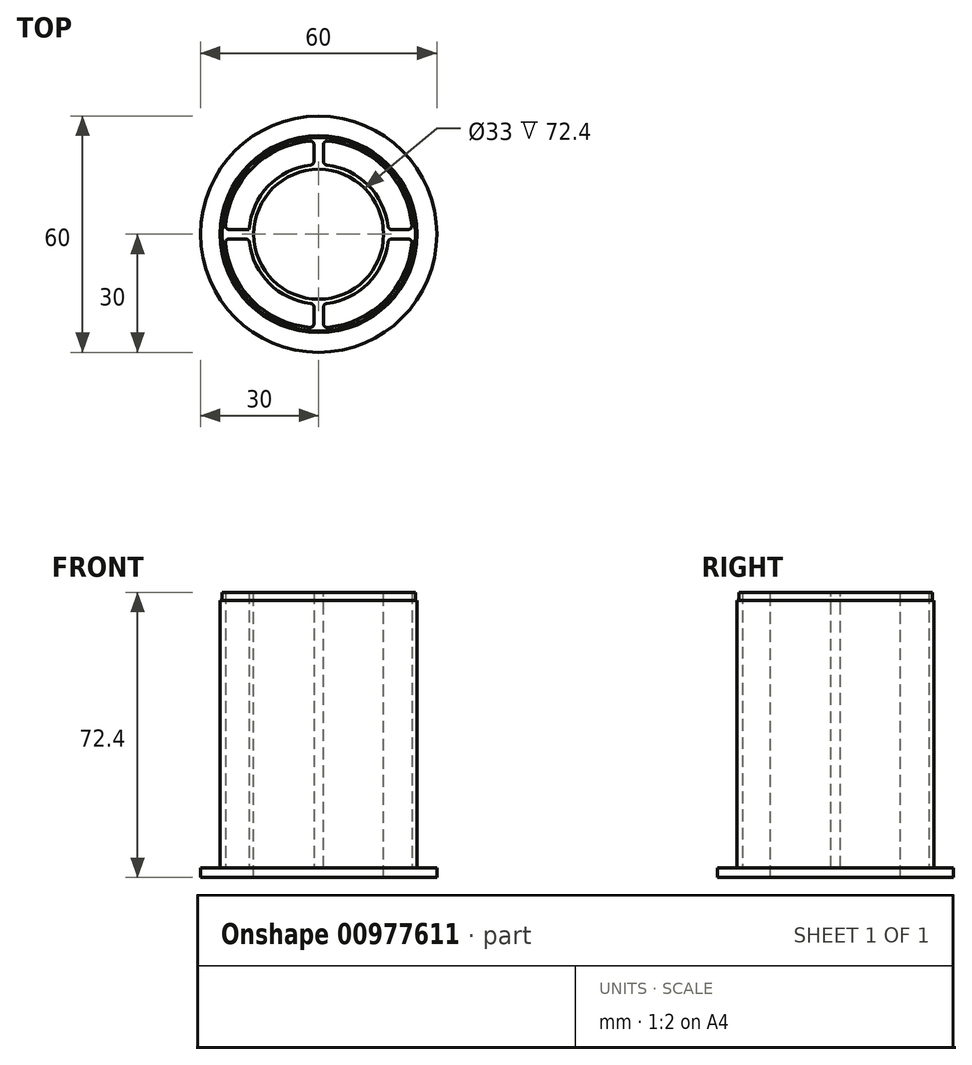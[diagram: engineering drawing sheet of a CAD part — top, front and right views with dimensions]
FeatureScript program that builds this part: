
annotation { "Feature Type Name" : "Feature", "Feature Type Description" : "" }
export const myFeature = defineFeature(function(context is Context, id is Id, definition is map)
    precondition{}
    {
        {
            var Q0;
            Q0=qCreatedBy(makeId("Top.planeOp"),FACE);
            var sketch = newSketch(context, id + "F0", { "sketchPlane" : qUnion([Q0])});
            skCircle(sketch, "E0", {"center": v(0, 0) * mm, "radius": 25 * mm});
            skCircle(sketch, "E1", {"center": v(0, 0) * mm, "radius": 16.5 * mm});
            skCircle(sketch, "E2", {"center": v(0, 0) * mm, "radius": 23.8 * mm});
            skPoint(sketch, "E3", {"position": v(0, 23.8) * mm});
            skPoint(sketch, "E4", {"position": v(0, 25) * mm});
            skCircle(sketch, "E5", {"center": v(0, 0) * mm, "radius": 17.7 * mm});
            skPoint(sketch, "E6", {"position": v(0, 16.5) * mm});
            skPoint(sketch, "E7", {"position": v(0, 17.7) * mm});
            skLineSegment(sketch, "E8", {"start": v(-1.2, 17.66) * mm, "end": v(-1.2, 23.77) * mm});
            skLineSegment(sketch, "E9", {"start": v(1.2, 17.66) * mm, "end": v(1.2, 23.77) * mm});
            skLineSegment(sketch, "E10.1.0", {"start": v(17.66, 1.2) * mm, "end": v(23.77, 1.2) * mm});
            skLineSegment(sketch, "E10.1.1", {"start": v(17.66, -1.2) * mm, "end": v(23.77, -1.2) * mm});
            skLineSegment(sketch, "E10.2.0", {"start": v(1.2, -17.66) * mm, "end": v(1.2, -23.77) * mm});
            skLineSegment(sketch, "E10.2.1", {"start": v(-1.2, -17.66) * mm, "end": v(-1.2, -23.77) * mm});
            skLineSegment(sketch, "E10.3.0", {"start": v(-17.66, -1.2) * mm, "end": v(-23.77, -1.2) * mm});
            skLineSegment(sketch, "E10.3.1", {"start": v(-17.66, 1.2) * mm, "end": v(-23.77, 1.2) * mm});
            skLineSegment(sketch, "E10.anchor1", {"start": v(0, 0) * mm, "end": v(-1.2, 17.66) * mm, "construction": true});
            skLineSegment(sketch, "E10.anchor2", {"start": v(0, 0) * mm, "end": v(-17.66, -1.2) * mm, "construction": true});
            skSolve(sketch);
        }
        {
            var Q0;
            Q0=qCreatedBy(makeId("Top.planeOp"),FACE);
            var sketch = newSketch(context, id + "F1", { "sketchPlane" : qUnion([Q0])});
            skCircle(sketch, "E11", {"center": v(0, 0) * mm, "radius": 30 * mm});
            skCircle(sketch, "E12.0", {"center": v(0, 0) * mm, "radius": 25 * mm, "construction": true});
            skPoint(sketch, "E13", {"position": v(0, -25) * mm});
            skPoint(sketch, "E14", {"position": v(0, -30) * mm});
            skCircle(sketch, "E15.0", {"center": v(0, 0) * mm, "radius": 16.5 * mm});
            skSolve(sketch);
        }
        {
            var Q0;
            Q0 = qSketchRegion(id + "F1", true);
            extrude(context, id + "F2", {"entities" : qUnion([Q0]), "oppositeDirection" : true, "depth" : 2.4 * mm, "offsetDistance" : 25 * mm});
        }
        {
            var Q0;
            Q0=makeQuery(id+"F0.imprint","IMPRINT",FACE,{"disambiguationData":[TD([[makeQuery(id+"F0.imprint","IMPRINT",EDGE,{"derivedFrom":sQuery(id+"F0.wireOp",EDGE,"E0")}),1.0]])]});
            var Q1;
            {var subQ0=sQuery(id+"F0.wireOp",EDGE,"E10.3.0");Q1=makeQuery(id+"F0.imprint","IMPRINT",FACE,{"disambiguationData":[TD([[makeQuery(id+"F0.imprint","IMPRINT",EDGE,{"derivedFrom":subQ0}),-1.0]])]});}
            var Q2;
            {var subQ0=sQuery(id+"F0.wireOp",EDGE,"E8");Q2=makeQuery(id+"F0.imprint","IMPRINT",FACE,{"disambiguationData":[TD([[makeQuery(id+"F0.imprint","IMPRINT",EDGE,{"derivedFrom":subQ0}),-1.0]])]});}
            var Q3;
            {var subQ0=sQuery(id+"F0.wireOp",EDGE,"E10.1.0");Q3=makeQuery(id+"F0.imprint","IMPRINT",FACE,{"disambiguationData":[TD([[makeQuery(id+"F0.imprint","IMPRINT",EDGE,{"derivedFrom":subQ0}),-1.0]])]});}
            var Q4;
            {var subQ0=sQuery(id+"F0.wireOp",EDGE,"E10.2.0");Q4=makeQuery(id+"F0.imprint","IMPRINT",FACE,{"disambiguationData":[TD([[makeQuery(id+"F0.imprint","IMPRINT",EDGE,{"derivedFrom":subQ0}),-1.0]])]});}
            var Q5;
            Q5=makeQuery(id+"F0.imprint","IMPRINT",FACE,{"disambiguationData":[TD([[makeQuery(id+"F0.imprint","IMPRINT",EDGE,{"derivedFrom":sQuery(id+"F0.wireOp",EDGE,"E1")}),-1.0]])]});
            extrude(context, id + "F3", {"entities" : qUnion([Q0, Q1, Q2, Q3, Q4, Q5]), "operationType" : NewBodyOperationType.ADD, "depth" : 70 * mm, "offsetDistance" : 25 * mm});
        }
        {
            var Q0;
            Q0=qCreatedBy(makeId("Front.planeOp"),FACE);
            var sketch = newSketch(context, id + "F4", { "sketchPlane" : qUnion([Q0])});
            skLineSegment(sketch, "E16", {"start": v(25, 70) * mm, "end": v(25, 0) * mm, "construction": true});
            skLineSegment(sketch, "E17.bottom", {"start": v(25, 70) * mm, "end": v(24.6, 70) * mm});
            skLineSegment(sketch, "E17.top", {"start": v(25, 68) * mm, "end": v(24.6, 68) * mm});
            skLineSegment(sketch, "E17.left", {"start": v(25, 70) * mm, "end": v(25, 68) * mm});
            skLineSegment(sketch, "E17.right", {"start": v(24.6, 70) * mm, "end": v(24.6, 68) * mm});
            skLineSegment(sketch, "E18", {"start": v(0, 0) * mm, "end": v(0, 82.8) * mm, "construction": true});
            skSolve(sketch);
        }
        {
            var Q0;
            Q0=makeQuery(id+"F4.imprint","IMPRINT",FACE,{"disambiguationData":[TD([[makeQuery(id+"F4.imprint","IMPRINT",EDGE,{"derivedFrom":sQuery(id+"F4.wireOp",EDGE,"E17.bottom")}),1.0]])]});
            var Q1;
            Q1=sQuery(id+"F4.wireOp",EDGE,"E17.left");
            var Q2;
            Q2=sQuery(id+"F4.wireOp",EDGE,"E17.bottom");
            var Q3;
            Q3=sQuery(id+"F4.wireOp",EDGE,"E17.right");
            var Q4;
            Q4=sQuery(id+"F4.wireOp",EDGE,"E17.top");
            var Q5;
            Q5=sQuery(id+"F4.wireOp",EDGE,"E18");
            revolve(context, id + "F5", {"operationType" : NewBodyOperationType.REMOVE, "surfaceOperationType" : NewSurfaceOperationType.NEW, "entities" : qUnion([Q0]), "surfaceEntities" : qUnion([Q1, Q2, Q3, Q4]), "axis" : qUnion([Q5]), "revolveType" : RevolveType.FULL, "oppositeDirection" : true});
        }
        {
            var Q0;
            Q0=makeQuery(id+"F3.opExtrude","SWEPT_EDGE",EDGE,{"disambiguationData":[OSD([sQuery(id+"F0.wireOp",EDGE,"E2"),sQuery(id+"F0.wireOp",EDGE,"E8")])]});
            var Q1;
            Q1=makeQuery(id+"F3.opExtrude","SWEPT_EDGE",EDGE,{"disambiguationData":[OSD([sQuery(id+"F0.wireOp",EDGE,"E5"),sQuery(id+"F0.wireOp",EDGE,"E8")])]});
            var Q2;
            Q2=makeQuery(id+"F3.opExtrude","SWEPT_EDGE",EDGE,{"disambiguationData":[OSD([sQuery(id+"F0.wireOp",EDGE,"E2"),sQuery(id+"F0.wireOp",EDGE,"E9")])]});
            var Q3;
            Q3=makeQuery(id+"F3.opExtrude","SWEPT_EDGE",EDGE,{"disambiguationData":[OSD([sQuery(id+"F0.wireOp",EDGE,"E5"),sQuery(id+"F0.wireOp",EDGE,"E9")])]});
            var Q4;
            Q4=makeQuery(id+"F3.opExtrude","SWEPT_EDGE",EDGE,{"disambiguationData":[OSD([sQuery(id+"F0.wireOp",EDGE,"E5"),sQuery(id+"F0.wireOp",EDGE,"E10.1.0")])]});
            var Q5;
            Q5=makeQuery(id+"F3.opExtrude","SWEPT_EDGE",EDGE,{"disambiguationData":[OSD([sQuery(id+"F0.wireOp",EDGE,"E5"),sQuery(id+"F0.wireOp",EDGE,"E10.1.1")])]});
            var Q6;
            Q6=makeQuery(id+"F3.opExtrude","SWEPT_EDGE",EDGE,{"disambiguationData":[OSD([sQuery(id+"F0.wireOp",EDGE,"E5"),sQuery(id+"F0.wireOp",EDGE,"E10.2.0")])]});
            var Q7;
            Q7=makeQuery(id+"F3.opExtrude","SWEPT_EDGE",EDGE,{"disambiguationData":[OSD([sQuery(id+"F0.wireOp",EDGE,"E5"),sQuery(id+"F0.wireOp",EDGE,"E10.2.1")])]});
            var Q8;
            Q8=makeQuery(id+"F3.opExtrude","SWEPT_EDGE",EDGE,{"disambiguationData":[OSD([sQuery(id+"F0.wireOp",EDGE,"E5"),sQuery(id+"F0.wireOp",EDGE,"E10.3.0")])]});
            var Q9;
            Q9=makeQuery(id+"F3.opExtrude","SWEPT_EDGE",EDGE,{"disambiguationData":[OSD([sQuery(id+"F0.wireOp",EDGE,"E2"),sQuery(id+"F0.wireOp",EDGE,"E10.2.0")])]});
            var Q10;
            Q10=makeQuery(id+"F3.opExtrude","SWEPT_EDGE",EDGE,{"disambiguationData":[OSD([sQuery(id+"F0.wireOp",EDGE,"E2"),sQuery(id+"F0.wireOp",EDGE,"E10.1.1")])]});
            var Q11;
            Q11=makeQuery(id+"F3.opExtrude","SWEPT_EDGE",EDGE,{"disambiguationData":[OSD([sQuery(id+"F0.wireOp",EDGE,"E2"),sQuery(id+"F0.wireOp",EDGE,"E10.1.0")])]});
            var Q12;
            Q12=makeQuery(id+"F3.opExtrude","SWEPT_EDGE",EDGE,{"disambiguationData":[OSD([sQuery(id+"F0.wireOp",EDGE,"E2"),sQuery(id+"F0.wireOp",EDGE,"E10.2.1")])]});
            var Q13;
            Q13=makeQuery(id+"F3.opExtrude","SWEPT_EDGE",EDGE,{"disambiguationData":[OSD([sQuery(id+"F0.wireOp",EDGE,"E2"),sQuery(id+"F0.wireOp",EDGE,"E10.3.0")])]});
            var Q14;
            Q14=makeQuery(id+"F3.opExtrude","SWEPT_EDGE",EDGE,{"disambiguationData":[OSD([sQuery(id+"F0.wireOp",EDGE,"E2"),sQuery(id+"F0.wireOp",EDGE,"E10.3.1")])]});
            fillet(context, id + "F6", {"entities" : qUnion([Q0, Q1, Q2, Q3, Q4, Q5, Q6, Q7, Q8, Q9, Q10, Q11, Q12, Q13, Q14]), "radius" : 1 * mm, "tangentPropagation" : true, "allowEdgeOverflow" : false});
        }
    });
